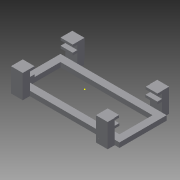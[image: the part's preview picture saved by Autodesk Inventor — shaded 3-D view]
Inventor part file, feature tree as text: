
AUTODESK INVENTOR PART (.ipt)
format: ipt  version: 2015 (Build 190159000, 159)  size: 209,408 bytes
history: native  units: mm
features: sketch x9, extrude x7
ambient origin geometry x8: Origin, YZ Plane, XZ Plane, XY Plane, X Axis, Y Axis, Z Axis, Center Point
bodies: Solid1 (feature_tree)
feature tree (16):
  extrude  "Extrusion1"  Depth=20.0mm
  sketch  "Sketch2"  dims[d2=3.0mm d3=3.0mm]
  extrude  "Extrusion2"  Depth=3.0mm
  extrude  "Extrusion3"  Depth=3.0mm
  sketch  "Sketch5"  dims[d9=2.0mm d10=5.0mm]
  extrude  "Extrusion4"  Depth=2.0mm
  extrude  "Extrusion5"  Depth=5.0mm
  extrude  "Extrusion6"  Depth=3.0mm TaperAngle=0.0deg
  extrude  "Extrusion7"  Depth=2.0mm
  sketch  "Sketch1"  dims[d0=45.0mm d1=20.0mm]
  sketch  "Sketch3"  dims[d4=3.0mm d5=3.0mm]
  sketch  "Sketch4"  dims[d6=2.0mm d7=0.0mm d8=2.0mm]
  sketch  "Sketch6"  dims[d11=5.0mm d12=3.0mm d13=0.0mm]
  sketch  "Sketch7"  dims[d14=2.0mm d15=2.0mm]
  sketch  "Sketch8"  dims[d16=5.0mm]
  sketch  "Sketch9"  dims[d17=5.0mm d18=3.0mm d19=0.0mm d20=8.0mm d21=0.0mm d22=1.0mm d23=1.0mm d24=2.0mm d25=0.0mm d26=1.0mm d27=2.0mm d28=2.0mm d29=0.0mm d30=1.0mm d31=2.0mm d32=1.0mm d33=2.0mm d34=0.0mm]
